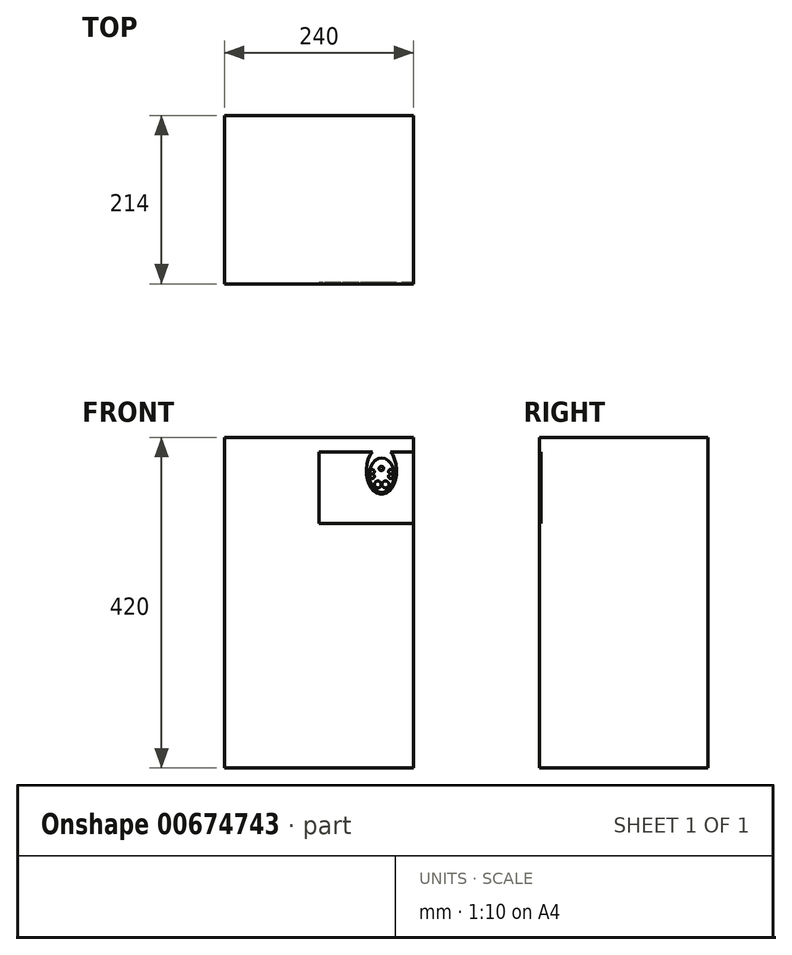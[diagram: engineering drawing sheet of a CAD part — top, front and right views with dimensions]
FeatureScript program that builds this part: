
annotation { "Feature Type Name" : "Feature", "Feature Type Description" : "" }
export const myFeature = defineFeature(function(context is Context, id is Id, definition is map)
    precondition{}
    {
        {
            var Q0;
            Q0=qCreatedBy(makeId("Front.planeOp"),FACE);
            var sketch = newSketch(context, id + "F0", { "sketchPlane" : qUnion([Q0])});
            skLineSegment(sketch, "E0.bottom", {"start": v(120, 210) * mm, "end": v(-120, 210) * mm});
            skLineSegment(sketch, "E0.top", {"start": v(120, -210) * mm, "end": v(-120, -210) * mm});
            skLineSegment(sketch, "E0.left", {"start": v(120, 210) * mm, "end": v(120, -210) * mm});
            skLineSegment(sketch, "E0.right", {"start": v(-120, 210) * mm, "end": v(-120, -210) * mm});
            skPoint(sketch, "E0.middle", {"position": v(0, 0) * mm});
            skSolve(sketch);
        }
        {
            var Q0;
            Q0=makeQuery(id+"F0.imprint","IMPRINT",FACE,{"disambiguationData":[TD([[makeQuery(id+"F0.imprint","IMPRINT",EDGE,{"derivedFrom":sQuery(id+"F0.wireOp",EDGE,"E0.bottom")}),1.0]])]});
            extrude(context, id + "F1", {"entities" : qUnion([Q0]), "depth" : 214 * mm, "offsetDistance" : 25 * mm});
        }
        {
            var Q0;
            Q0=makeQuery(id+"F1.opExtrude","CAP_FACE",FACE,{"disambiguationData":[OSD([sQuery(id+"F0.wireOp",EDGE,"E0.bottom"),sQuery(id+"F0.wireOp",EDGE,"E0.top"),sQuery(id+"F0.wireOp",EDGE,"E0.left"),sQuery(id+"F0.wireOp",EDGE,"E0.right")])],"isStart":false});
            var sketch = newSketch(context, id + "F2", { "sketchPlane" : qUnion([Q0])});
            skEllipse(sketch, "E1", {"center": v(79.64, 162) * mm, "majorRadius": 21.83 * mm, "minorRadius": 16.04 * mm, "majorAxis": v(0, 1)});
            skEllipse(sketch, "E2", {"center": v(79.36, 167.65) * mm, "majorRadius": 29.93 * mm, "minorRadius": 19.27 * mm, "majorAxis": v(0, 1)});
            skCircle(sketch, "E3", {"center": v(74.76, 150.26) * mm, "radius": 4.32 * mm});
            skCircle(sketch, "E4.MirrorC", {"center": v(84.52, 150.26) * mm, "radius": 4.32 * mm});
            skCircle(sketch, "E5", {"center": v(67.51, 160.52) * mm, "radius": 2.8 * mm});
            skCircle(sketch, "E6.MirrorC", {"center": v(67.51, 166.51) * mm, "radius": 2.8 * mm});
            skCircle(sketch, "E7.MirrorC", {"center": v(91.22, 160.52) * mm, "radius": 2.8 * mm});
            skCircle(sketch, "E8.MirrorC", {"center": v(91.22, 166.51) * mm, "radius": 2.8 * mm});
            skCircle(sketch, "E9", {"center": v(79.36, 170.55) * mm, "radius": 2.85 * mm});
            skLineSegment(sketch, "E10", {"start": v(-120, 89.19) * mm, "end": v(120, 89.19) * mm});
            skLineSegment(sketch, "E11.bottom", {"start": v(120, 191.8) * mm, "end": v(0, 191.8) * mm});
            skLineSegment(sketch, "E11.top", {"start": v(120, 100.98) * mm, "end": v(0, 100.98) * mm});
            skLineSegment(sketch, "E11.left", {"start": v(120, 191.8) * mm, "end": v(120, 100.98) * mm});
            skLineSegment(sketch, "E11.right", {"start": v(0, 191.8) * mm, "end": v(0, 100.98) * mm});
            skSolve(sketch);
        }
        {
            var Q0;
            Q0=makeQuery(id+"F2.imprint","IMPRINT",FACE,{"disambiguationData":[TD([[makeQuery(id+"F2.imprint","IMPRINT",EDGE,{"derivedFrom":sQuery(id+"F2.wireOp",EDGE,"E1")}),1.0]])]});
            var Q1;
            Q1=makeQuery(id+"F2.imprint","IMPRINT",FACE,{"disambiguationData":[TD([[makeQuery(id+"F2.imprint","IMPRINT",EDGE,{"derivedFrom":sQuery(id+"F2.wireOp",EDGE,"E11.top")}),-1.0]])]});
            extrude(context, id + "F3", {"entities" : qUnion([Q0, Q1]), "operationType" : NewBodyOperationType.REMOVE, "oppositeDirection" : true, "depth" : 2 * mm, "offsetDistance" : 25 * mm});
        }
    });
